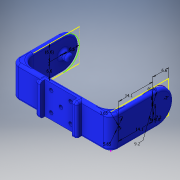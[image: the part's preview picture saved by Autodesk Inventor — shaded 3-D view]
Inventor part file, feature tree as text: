
AUTODESK INVENTOR PART (.ipt)
format: ipt  version: 2016 (Build 200138000, 138)  size: 416,256 bytes
history: native  units: in
note: dims shown in document units (in); Inventor stores cm internally (conversion verified against a paired STEP export)
features: fillet x13, extrude x8, sketch x8, hole x1
ambient origin geometry x8: Origin, YZ Plane, XZ Plane, XY Plane, X Axis, Y Axis, Z Axis, Center Point
bodies: Solid1 (feature_tree)
feature tree (30):
  extrude  "Extrusion1"  Depth=0.5197in
  extrude  "Extrusion3"  Depth=0.0787in
  sketch  "Sketch5"  dims[d9=0.9449in d10=0.0in d11=0.2835in]
  extrude  "Extrusion4"  Depth=0.2835in
  extrude  "Extrusion5"  Depth=0.5197in
  fillet  "Fillet1"  Radius=0.2598in
  fillet  "Fillet4"  Radius=0.5197in
  fillet  "Fillet5"  Radius=0.3622in
  fillet  "Fillet6"  Radius=0.1437in
  fillet  "Fillet7"  Radius=0.5551in
  extrude  "Extrusion6"  Depth=0.0787in TaperAngle=0.0deg
  fillet  "Fillet8"  Radius=0.0787in
  fillet  "Fillet9"  Radius=0.0787in
  sketch  "Sketch9"  dims[d19=0.2224in d24=0.0787in d25=0.0in d26=0.0787in d27=0.0787in]
  extrude  "Extrusion7"  Depth=0.1969in
  fillet  "Fillet10"  Radius=0.0394in
  fillet  "Fillet11"  Radius=0.0394in
  sketch  "Sketch10"  dims[d28=0.0787in d29=0.0in d30=0.1969in d33=0.0394in d34=0.0394in]
  extrude  "Extrusion8"  Depth=0.0197in
  fillet  "Fillet12"  Radius=0.0787in
  extrude  "Extrusion9"  Depth=0.1969in
  fillet  "Fillet14"  Radius=0.0394in
  hole  "Hole1"  [1 undecoded]
  fillet  "Fillet15"  Radius=0.2598in
  fillet  "Fillet16"  Radius=0.2598in
  sketch  "Sketch1"  dims[d0=1.6142in d1=0.5197in]
  sketch  "Sketch4"  dims[d2=0.0787in d3=0.0in d8=0.0787in]
  sketch  "Sketch7"  dims[d12=0.2598in d13=0.2598in d14=0.2598in d15=0.5197in d16=0.3622in d17=0.1437in d18=0.5551in]
  sketch  "Sketch11"  dims[d35=0.0394in d36=0.0197in d37=0.0787in]
  sketch  "Sketch14"  dims[d38=0.9449in d39=0.0in d40=0.1969in d41=0.0394in d43=0.2598in d44=0.2598in d45=0.2598in d46=0.1181in d47=0.1181in d48=0.0in d49=0.0394in d50=0.0394in d51=0.1181in d52=0.1181in d53=0.0in d54=0.0394in d56=0.5197in d57=0.5472in d58=0.5472in d59=0.0787in d60=0.0787in d61=0.0787in d62=0.0in d63=0.0394in d66=0.2598in d67=0.2598in d68=0.2598in d69=0.2598in d70=0.315in d71=0.315in d72=0.0591in d73=0.2362in d74=0.1575in d75=0.0787in d76=90.0deg d77=0.315in d78=0.8108in d79=0.1181in d80=0.0394in d81=0.5551in]
note: 1 required parameter value undecoded (feature->parameter linkage not recoverable at this tier; creation-order binding heuristic only, values carry confidence <= 0.55)
